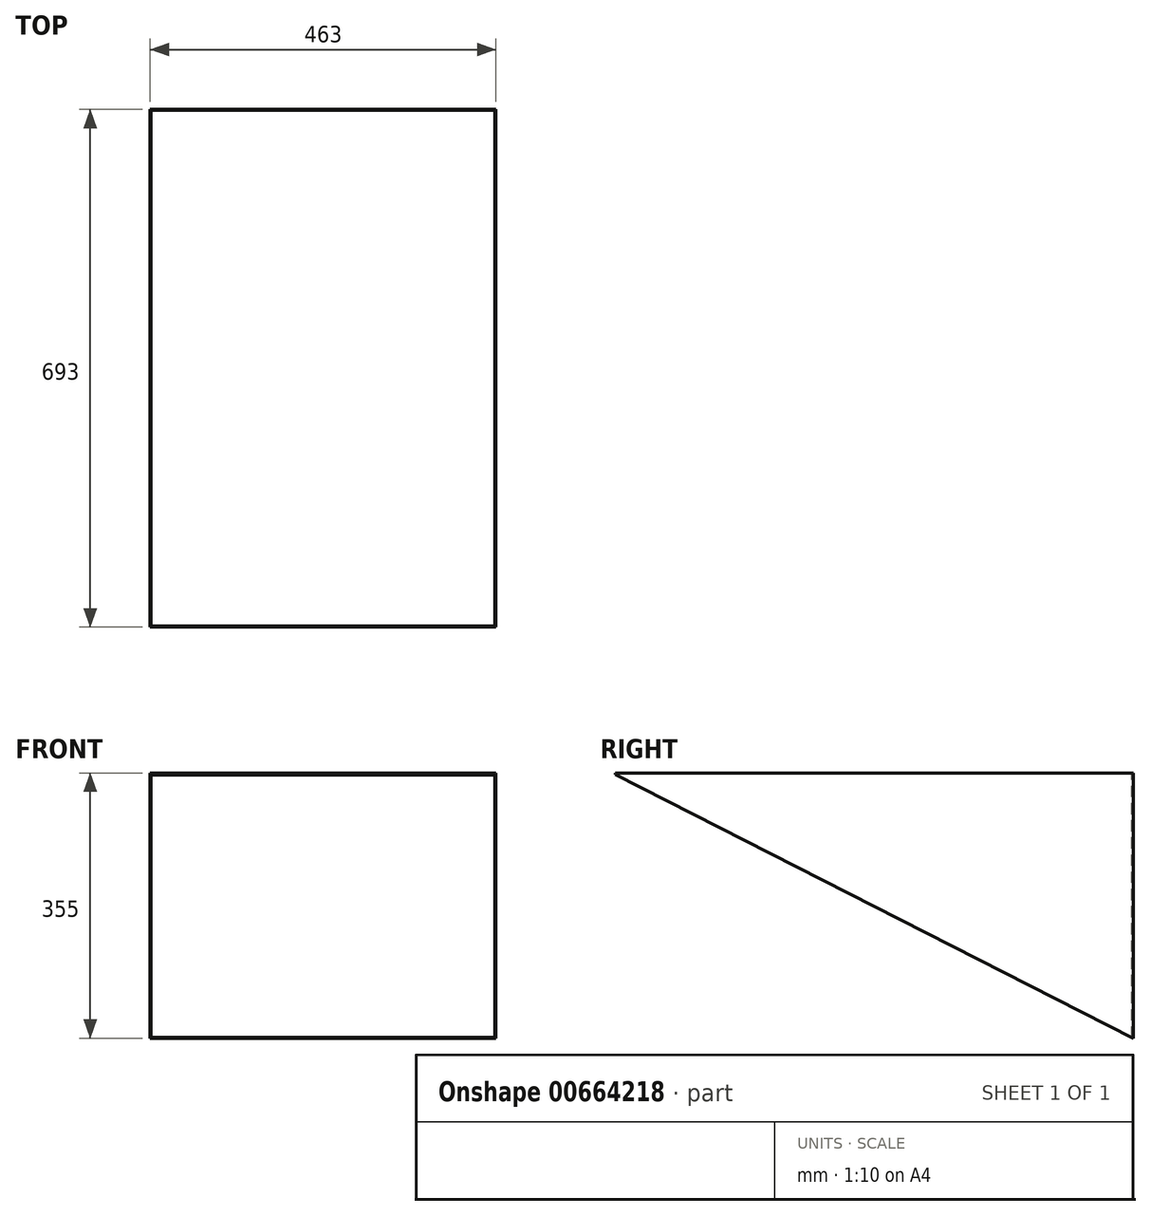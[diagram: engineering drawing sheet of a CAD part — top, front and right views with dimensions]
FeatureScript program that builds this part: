
annotation { "Feature Type Name" : "Feature", "Feature Type Description" : "" }
export const myFeature = defineFeature(function(context is Context, id is Id, definition is map)
    precondition{}
    {
        {
            var Q0;
            Q0=qCreatedBy(makeId("Top.planeOp"),FACE);
            var sketch = newSketch(context, id + "F0", { "sketchPlane" : qUnion([Q0])});
            skLineSegment(sketch, "E0.bottom", {"start": v(230, -345) * mm, "end": v(-230, -345) * mm});
            skLineSegment(sketch, "E0.top", {"start": v(230, 345) * mm, "end": v(-230, 345) * mm});
            skLineSegment(sketch, "E0.left", {"start": v(230, -345) * mm, "end": v(230, 345) * mm});
            skLineSegment(sketch, "E0.right", {"start": v(-230, -345) * mm, "end": v(-230, 345) * mm});
            skPoint(sketch, "E0.middle", {"position": v(0, 0) * mm});
            skLineSegment(sketch, "E1.0", {"start": v(231.5, 346.5) * mm, "end": v(-231.5, 346.5) * mm});
            skLineSegment(sketch, "E1.1", {"start": v(231.5, -346.5) * mm, "end": v(231.5, 346.5) * mm});
            skLineSegment(sketch, "E1.2", {"start": v(231.5, -346.5) * mm, "end": v(-231.5, -346.5) * mm});
            skLineSegment(sketch, "E1.3", {"start": v(-231.5, -346.5) * mm, "end": v(-231.5, 346.5) * mm});
            skSolve(sketch);
        }
        {
            var Q0;
            Q0=makeQuery(id+"F0.imprint","IMPRINT",FACE,{"disambiguationData":[TD([[makeQuery(id+"F0.imprint","IMPRINT",EDGE,{"derivedFrom":sQuery(id+"F0.wireOp",EDGE,"E0.bottom")}),1.0]])]});
            extrude(context, id + "F1", {"entities" : qUnion([Q0]), "oppositeDirection" : true, "depth" : 355 * mm, "offsetDistance" : 25 * mm});
        }
        {
            var Q0;
            Q0=makeQuery(id+"F1.opExtrude","SWEPT_FACE",FACE,{"disambiguationData":[OSD([sQuery(id+"F0.wireOp",EDGE,"E1.1")])]});
            var sketch = newSketch(context, id + "F2", { "sketchPlane" : qUnion([Q0])});
            skLineSegment(sketch, "E2", {"start": v(-346.5, 0) * mm, "end": v(-346.5, -2) * mm});
            skLineSegment(sketch, "E3", {"start": v(-346.5, -2) * mm, "end": v(346.5, -355) * mm});
            skSolve(sketch);
        }
        {
            var Q0;
            {var subQ0=sQuery(id+"F2.wireOp",EDGE,"E3");Q0=makeQuery(id+"F2.imprint","IMPRINT",FACE,{"disambiguationData":[TD([[makeQuery(id+"F2.imprint","IMPRINT",EDGE,{"derivedFrom":subQ0}),-1.0]])]});}
            extrude(context, id + "F3", {"entities" : qUnion([Q0]), "operationType" : NewBodyOperationType.REMOVE, "endBound" : BoundingType.THROUGH_ALL, "oppositeDirection" : true, "depth" : 25 * mm, "offsetDistance" : 25 * mm});
        }
        {
            var Q0;
            Q0=qCreatedBy(makeId("Right.planeOp"),FACE);
            var sketch = newSketch(context, id + "F4", { "sketchPlane" : qUnion([Q0])});
            skLineSegment(sketch, "E4", {"start": v(0, 0) * mm, "end": v(0, -178.55) * mm});
            skLineSegment(sketch, "E5", {"start": v(0, -178.55) * mm, "end": v(-1892, -178.55) * mm});
            skLineSegment(sketch, "E6", {"start": v(-1892, -178.55) * mm, "end": v(-1892, -861.55) * mm});
            skLineSegment(sketch, "E7", {"start": v(-1892, -861.55) * mm, "end": v(0, -178.55) * mm});
            skSolve(sketch);
        }
        {
            var Q0;
            Q0=sQuery(id+"F4.wireOp",VERTEX,"E7.start");
            var Q1;
            Q1=sQuery(id+"F4.wireOp",EDGE,"E7");
            cPlane(context, id + "F5", {"entities" : qUnion([Q0, Q1]), "cplaneType" : CPlaneType.LINE_POINT, "offset" : 25 * mm, "width" : 150 * mm, "height" : 150 * mm});
        }
    });
